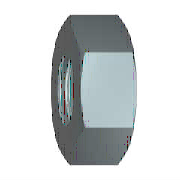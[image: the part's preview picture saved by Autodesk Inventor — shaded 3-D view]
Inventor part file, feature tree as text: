
AUTODESK INVENTOR PART (.ipt)
format: ipt  version: 2023.2 (Build 272271030, 271C)  size: 164,864 bytes
history: native  units: mm (DEFAULTED — no unit token found)
features: sketch x3, chamfer x1, hole x1, other x1, plane x1
ambient origin geometry x7: Origin, YZ Plane, XZ Plane, X Axis, Y Axis, Z Axis, Center Point
bodies: Solid1 (feature_tree), Body (feature_tree)
feature tree (7):
  chamfer  "Chamfer1"  Angle=30.0deg  [1 undecoded]
  hole  "Thread"  [1 undecoded]
  other  "Work Axis1"
  plane  "Work Plane1"
  sketch  "Sketch1"  dims[d0=31.176915mm]
  sketch  "Sketch2"  dims[d1=17.6mm]
  sketch  "Sketch3"  dims[d2=0.0mm d3=30.0deg d4=30.0deg d5=24.85mm d6=24.85mm d7=90.0deg d25=16.376mm d26=6.0mm d27=4.0mm d28=2.0mm d29=14.3117mm d30=8.0mm d31=20.594885mm d8=0.811899mm d9=30.0deg d10=0.811899mm d11=30.0deg d13=0.0mm d14=0.0mm d39=0.0mm d40=0.811899mm d41=0.811899mm d42=0.0mm]
note: 2 required parameter values undecoded (feature->parameter linkage not recoverable at this tier; creation-order binding heuristic only, values carry confidence <= 0.55)
